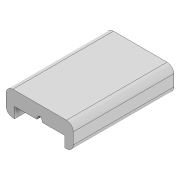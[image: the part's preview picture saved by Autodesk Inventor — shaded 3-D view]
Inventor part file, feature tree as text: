
AUTODESK INVENTOR PART (.ipt)
format: ipt  version: 2022 (Build 260153000, 153)  size: 117,248 bytes
history: native  units: mm
features: extrude x2, sketch x2, fillet x1
ambient origin geometry x8: Origin, YZ Plane, XZ Plane, XY Plane, X Axis, Y Axis, Z Axis, Center Point
bodies: Solid1 (feature_tree)
feature tree (5):
  extrude  "Extrusion1"  Depth=7.5mm
  fillet  "Fillet1"  Radius=3.75mm
  extrude  "Extrusion2"  Depth=1.0mm
  sketch  "Sketch1"  dims[d0=10.0mm d1=7.5mm d2=3.75mm]
  sketch  "Sketch2"  dims[d3=5.0mm d4=1.0mm d5=0.6mm d6=0.6mm d7=1.5mm d8=12.217305mm d9=12.217305mm d10=15.0mm d11=0.0mm d12=1.0mm d13=100.0mm d14=0.0mm]
